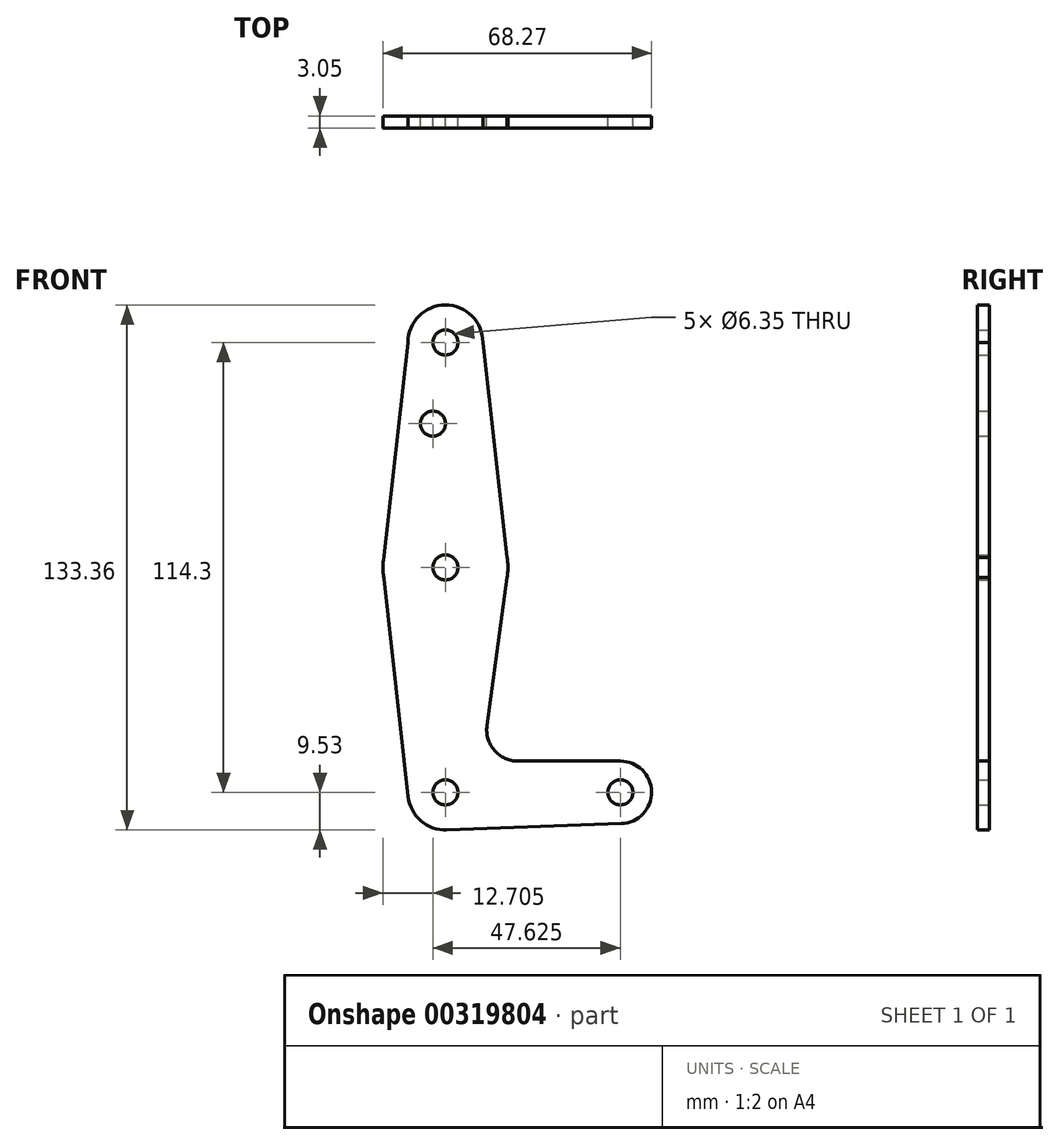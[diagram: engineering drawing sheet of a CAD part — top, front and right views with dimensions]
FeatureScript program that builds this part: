
annotation { "Feature Type Name" : "Feature", "Feature Type Description" : "" }
export const myFeature = defineFeature(function(context is Context, id is Id, definition is map)
    precondition{}
    {
        {
            var Q0;
            Q0=qCreatedBy(makeId("Front.planeOp"),FACE);
            var sketch = newSketch(context, id + "F0", { "sketchPlane" : qUnion([Q0])});
            skPoint(sketch, "E0.center.orphan", {"position": v(0, 57.15) * mm});
            skPoint(sketch, "E1.center.orphan", {"position": v(0, 0) * mm});
            skPoint(sketch, "E2.end.orphan", {"position": v(44.45, 0) * mm});
            skPoint(sketch, "E3.start.orphan", {"position": v(0, 114.3) * mm});
            skPoint(sketch, "E4.center.orphan", {"position": v(0, 57.1) * mm});
            skCircle(sketch, "E5", {"center": v(0, 0) * mm, "radius": 9.53 * mm});
            skCircle(sketch, "E6", {"center": v(44.45, 0) * mm, "radius": 7.94 * mm});
            skCircle(sketch, "E7", {"center": v(0, 57.15) * mm, "radius": 15.88 * mm});
            skCircle(sketch, "E8", {"center": v(0, 114.3) * mm, "radius": 9.53 * mm});
            skLineSegment(sketch, "E9", {"start": v(0, 104.78) * mm, "end": v(0, 0) * mm});
            skLineSegment(sketch, "E10", {"start": v(-9.53, 114.3) * mm, "end": v(-15.77, 58.93) * mm});
            skLineSegment(sketch, "E11", {"start": v(9.52, 114.3) * mm, "end": v(15.67, 59.69) * mm});
            skLineSegment(sketch, "E12", {"start": v(-15.6, 54.21) * mm, "end": v(-9.47, -1.05) * mm});
            skLineSegment(sketch, "E13", {"start": v(15.67, 54.61) * mm, "end": v(10.56, 16.96) * mm});
            skLineSegment(sketch, "E14", {"start": v(18.44, 7.94) * mm, "end": v(44.45, 7.94) * mm});
            skCircle(sketch, "E15", {"center": v(0, 114.3) * mm, "radius": 3.18 * mm});
            skCircle(sketch, "E16", {"center": v(0, 57.15) * mm, "radius": 3.18 * mm});
            skCircle(sketch, "E17", {"center": v(0, 0) * mm, "radius": 3.18 * mm});
            skCircle(sketch, "E18", {"center": v(-3.17, 93.68) * mm, "radius": 3.18 * mm});
            skCircle(sketch, "E19", {"center": v(44.45, 0) * mm, "radius": 3.18 * mm});
            skArc(sketch, "E20.filletArc", {"start": v(10.56, 16.96) * mm, "mid": v(12.45, 10.66) * mm, "end": v(18.44, 7.94) * mm});
            skLineSegment(sketch, "E21", {"start": v(0, 0) * mm, "end": v(44.45, 0) * mm});
            skLineSegment(sketch, "E22", {"start": v(44.73, -7.93) * mm, "end": v(0.34, -9.52) * mm});
            skSolve(sketch);
        }
        {
            var Q0;
            Q0 = qSketchRegion(id + "F0", true);
            var Q1;
            {var subQ0=sQuery(id+"F0.wireOp",EDGE,"E9");var subQ1=sQuery(id+"F0.wireOp",EDGE,"E5");var subQ2=makeQuery(id+"F0.imprint","INTERSECT",VERTEX,{"derivedFrom":[subQ1,subQ0]});Q1=makeQuery(id+"F0.imprint","IMPRINT",FACE,{"disambiguationData":[TD([[makeQuery(id+"F0.imprint","IMPRINT",EDGE,{"disambiguationData":[TD([[subQ2,1.0]])],"derivedFrom":subQ1}),1.0]])]});}
            extrude(context, id + "F1", {"entities" : qUnion([Q0, Q1]), "depth" : 3.05 * mm});
        }
    });
